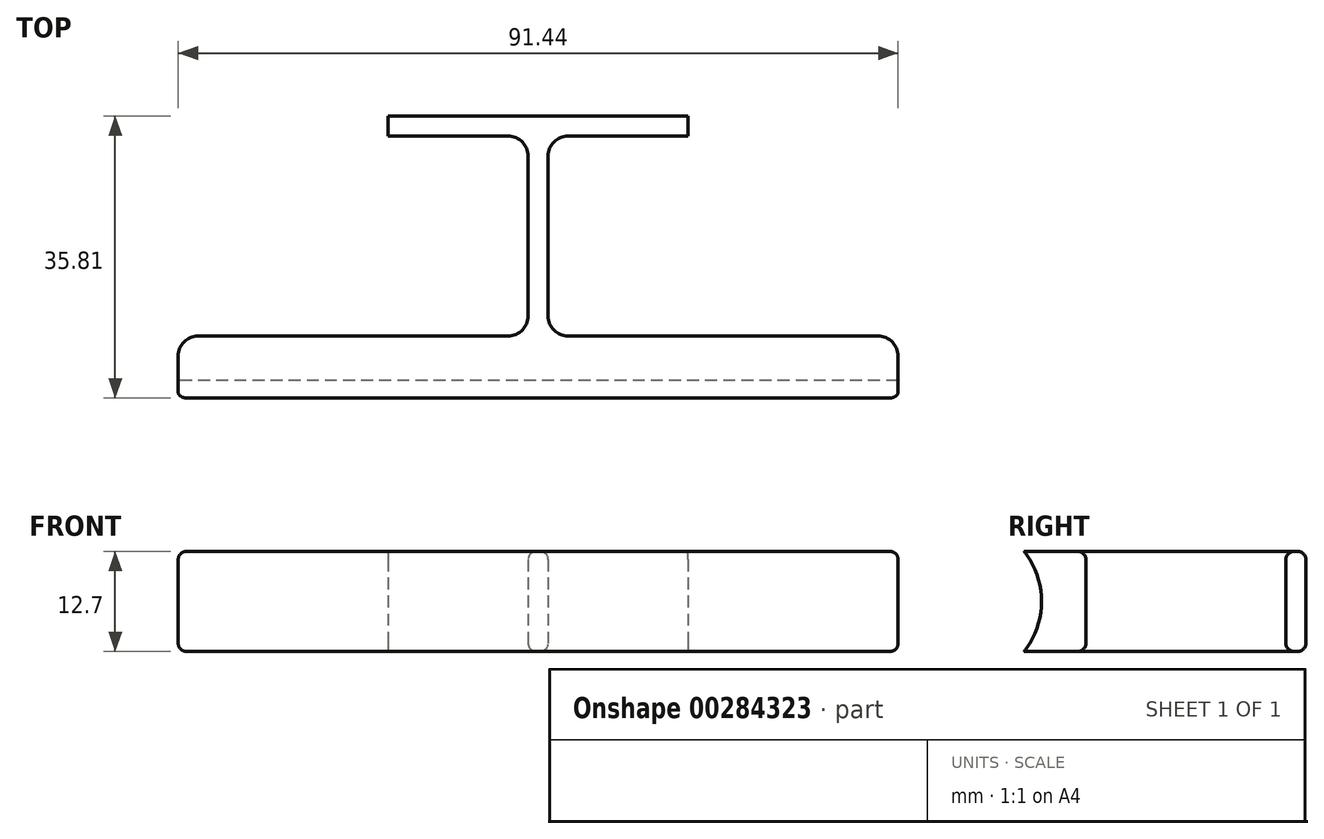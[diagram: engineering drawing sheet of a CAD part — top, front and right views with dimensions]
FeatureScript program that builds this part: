
annotation { "Feature Type Name" : "Feature", "Feature Type Description" : "" }
export const myFeature = defineFeature(function(context is Context, id is Id, definition is map)
    precondition{}
    {
        {
            var Q0;
            Q0=qCreatedBy(makeId("Top.planeOp"),FACE);
            var sketch = newSketch(context, id + "F0", { "sketchPlane" : qUnion([Q0])});
            skLineSegment(sketch, "E0", {"start": v(0, 0) * mm, "end": v(-19.05, 0) * mm});
            skLineSegment(sketch, "E1", {"start": v(0, 0) * mm, "end": v(19.05, 0) * mm});
            skLineSegment(sketch, "E2", {"start": v(-45.72, -27.94) * mm, "end": v(-45.72, -30.48) * mm});
            skLineSegment(sketch, "E3", {"start": v(-45.72, -30.48) * mm, "end": v(45.72, -30.48) * mm});
            skLineSegment(sketch, "E4", {"start": v(45.72, -30.48) * mm, "end": v(45.72, -27.94) * mm});
            skLineSegment(sketch, "E5", {"start": v(0, -30.48) * mm, "end": v(0, 0) * mm, "construction": true});
            skLineSegment(sketch, "E6.bottom", {"start": v(-19.05, -2.54) * mm, "end": v(-1.27, -2.54) * mm});
            skLineSegment(sketch, "E6.top", {"start": v(-45.72, -27.94) * mm, "end": v(-1.27, -27.94) * mm});
            skLineSegment(sketch, "E7", {"start": v(0, -2.54) * mm, "end": v(0, -27.94) * mm, "construction": true});
            skPoint(sketch, "E8", {"position": v(0, -15.24) * mm});
            skLineSegment(sketch, "E9.left", {"start": v(-1.27, -2.54) * mm, "end": v(-1.27, -27.94) * mm});
            skLineSegment(sketch, "E9.right", {"start": v(1.27, -2.54) * mm, "end": v(1.27, -27.94) * mm});
            skLineSegment(sketch, "E10", {"start": v(-1.27, -15.24) * mm, "end": v(1.27, -15.24) * mm, "construction": true});
            skLineSegment(sketch, "E11", {"start": v(-19.05, -2.54) * mm, "end": v(-19.05, 0) * mm});
            skLineSegment(sketch, "E12", {"start": v(19.05, 0) * mm, "end": v(19.05, -2.54) * mm});
            skLineSegment(sketch, "E13", {"start": v(-19.05, -1.27) * mm, "end": v(19.05, -1.27) * mm, "construction": true});
            skPoint(sketch, "E14", {"position": v(0, -1.27) * mm});
            skLineSegment(sketch, "E15.trimOffspring", {"start": v(1.27, -27.94) * mm, "end": v(45.72, -27.94) * mm});
            skLineSegment(sketch, "E16.trimOffspring", {"start": v(1.27, -2.54) * mm, "end": v(19.05, -2.54) * mm});
            skSolve(sketch);
        }
        {
            var Q0;
            Q0=makeQuery(id+"F0.imprint","IMPRINT",FACE,{"disambiguationData":[TD([[makeQuery(id+"F0.imprint","IMPRINT",EDGE,{"derivedFrom":sQuery(id+"F0.wireOp",EDGE,"E0")}),1.0]])]});
            extrude(context, id + "F1", {"entities" : qUnion([Q0]), "depth" : 12.7 * mm});
        }
        {
            var Q0;
            Q0=makeQuery(id+"F1.opExtrude","SWEPT_FACE",FACE,{"disambiguationData":[OSD([sQuery(id+"F0.wireOp",EDGE,"E4")])]});
            var sketch = newSketch(context, id + "F2", { "sketchPlane" : qUnion([Q0])});
            skLineSegment(sketch, "E17.0.0", {"start": v(-30.48, 0) * mm, "end": v(-27.94, 0) * mm});
            skLineSegment(sketch, "E17.0.2", {"start": v(-27.94, 12.7) * mm, "end": v(-30.48, 12.7) * mm});
            skLineSegment(sketch, "E17.0.3", {"start": v(-30.48, 12.7) * mm, "end": v(-30.48, 0) * mm});
            skLineSegment(sketch, "E18", {"start": v(-30.48, 0) * mm, "end": v(-35.8, 0) * mm});
            skLineSegment(sketch, "E19", {"start": v(-35.8, 0) * mm, "end": v(-30.48, 6.35) * mm});
            skLineSegment(sketch, "E20", {"start": v(-30.48, 6.35) * mm, "end": v(-35.8, 12.7) * mm});
            skLineSegment(sketch, "E21", {"start": v(-35.8, 12.7) * mm, "end": v(-30.48, 12.7) * mm});
            skSolve(sketch);
        }
        {
            var Q0;
            {var subQ2=sQuery(id+"F2.wireOp",EDGE,"E20");Q0=makeQuery(id+"F2.imprint","IMPRINT",FACE,{"disambiguationData":[TD([[makeQuery(id+"F2.imprint","IMPRINT",EDGE,{"derivedFrom":subQ2}),-1.0]])]});}
            var Q1;
            {var subQ0=sQuery(id+"F2.wireOp",EDGE,"E18");Q1=makeQuery(id+"F2.imprint","IMPRINT",FACE,{"disambiguationData":[TD([[makeQuery(id+"F2.imprint","IMPRINT",EDGE,{"derivedFrom":subQ0}),-1.0]])]});}
            var Q2;
            {var subQ0=sQuery(id+"F2.wireOp",EDGE,"DFXXT5Bl-ABkD-rZfx-TB3P-CU2xxBPRpCpw");var subQ1=sQuery(id+"F2.wireOp",EDGE,"E17.0.1");var subQ2=sQuery(id+"F2.wireOp",EDGE,"PkzQklKV-4UNx-XqyM-r72F-WXmGYkbQ70ns");var subQ3=sQuery(id+"F2.wireOp",EDGE,"ZFFAAHI1-nbwh-nJH1-ukWo-Dj7Sew2PWv25");Q2=makeQuery(id+"FTnoA9OfPemPWEm_1.1.Fb3Mo2sl9pyBsOD_1.boolean.opBoolean","MERGE",FACE,{"derivedFrom":[makeQuery(id+"F1.opExtrude","SWEPT_FACE",FACE,{"disambiguationData":[OSD([sQuery(id+"F0.wireOp",EDGE,"E2")])]}),makeQuery(id+"FTnoA9OfPemPWEm_1.1.Fb3Mo2sl9pyBsOD_1.opExtrude","CAP_FACE",FACE,{"disambiguationData":[OSD([subQ1,sQuery(id+"F2.wireOp",EDGE,"DQoqX5bU-sU3v-EXNl-5AFO-wBolTAnTBgKw"),subQ3])],"isStart":true}),makeQuery(id+"FTnoA9OfPemPWEm_1.1.Fb3Mo2sl9pyBsOD_1.opExtrude","CAP_FACE",FACE,{"disambiguationData":[OSD([subQ1,subQ3,subQ2])],"isStart":true}),makeQuery(id+"FTnoA9OfPemPWEm_1.1.Fb3Mo2sl9pyBsOD_1.opExtrude","CAP_FACE",FACE,{"disambiguationData":[OSD([subQ1,subQ2,subQ0])],"isStart":true}),makeQuery(id+"FTnoA9OfPemPWEm_1.1.Fb3Mo2sl9pyBsOD_1.opExtrude","CAP_FACE",FACE,{"disambiguationData":[OSD([subQ1,subQ0,sQuery(id+"F2.wireOp",EDGE,"Y51H4d37-WT34-3JM8-DEph-uDnF3JEXPVEw")])],"isStart":true})]});}
            extrude(context, id + "F3", {"entities" : qUnion([Q0, Q1]), "operationType" : NewBodyOperationType.ADD, "endBound" : BoundingType.UP_TO_SURFACE, "oppositeDirection" : true, "endBoundEntityFace" : qUnion([Q2]), "depth" : 101.6 * mm});
        }
        {
            var Q0;
            {var subQ0=sQuery(id+"F2.wireOp",EDGE,"E19");var subQ1=sQuery(id+"F2.wireOp",EDGE,"E17.0.3");var subQ2=sQuery(id+"F2.wireOp",EDGE,"E20");Q0=makeQuery(id+"F3.boolean.opBoolean","MERGE",EDGE,{"derivedFrom":[makeQuery(id+"F3.opExtrude","SWEPT_EDGE",EDGE,{"disambiguationData":[OSD([subQ1,subQ0,subQ2]),ownerDisambiguation([makeQuery(id+"F3.opExtrude","SWEPT_BODY",BODY,{"disambiguationData":[OSD([subQ1,subQ2,sQuery(id+"F2.wireOp",EDGE,"E21")])]})])]}),makeQuery(id+"F3.opExtrude","SWEPT_EDGE",EDGE,{"disambiguationData":[OSD([subQ1,subQ0,subQ2]),ownerDisambiguation([makeQuery(id+"F3.opExtrude","SWEPT_BODY",BODY,{"disambiguationData":[OSD([subQ1,sQuery(id+"F2.wireOp",EDGE,"E18"),subQ0])]})])]})]});}
            fillet(context, id + "F4", {"entities" : qUnion([Q0]), "radius" : 10.16 * mm, "tangentPropagation" : true, "allowEdgeOverflow" : false});
        }
        {
            var Q0;
            Q0=makeQuery(id+"F1.opExtrude","SWEPT_EDGE",EDGE,{"disambiguationData":[OSD([sQuery(id+"F0.wireOp",EDGE,"E6.bottom"),sQuery(id+"F0.wireOp",EDGE,"E9.left")])]});
            var Q1;
            Q1=makeQuery(id+"F1.opExtrude","SWEPT_EDGE",EDGE,{"disambiguationData":[OSD([sQuery(id+"F0.wireOp",EDGE,"E9.right"),sQuery(id+"F0.wireOp",EDGE,"E16.trimOffspring")])]});
            var Q2;
            Q2=makeQuery(id+"F1.opExtrude","SWEPT_EDGE",EDGE,{"disambiguationData":[OSD([sQuery(id+"F0.wireOp",EDGE,"E9.right"),sQuery(id+"F0.wireOp",EDGE,"E15.trimOffspring")])]});
            var Q3;
            Q3=makeQuery(id+"F1.opExtrude","SWEPT_EDGE",EDGE,{"disambiguationData":[OSD([sQuery(id+"F0.wireOp",EDGE,"E6.top"),sQuery(id+"F0.wireOp",EDGE,"E9.left")])]});
            var Q4;
            Q4=makeQuery(id+"F1.opExtrude","SWEPT_EDGE",EDGE,{"disambiguationData":[OSD([sQuery(id+"F0.wireOp",EDGE,"E2"),sQuery(id+"F0.wireOp",EDGE,"E6.top")])]});
            var Q5;
            Q5=makeQuery(id+"F1.opExtrude","SWEPT_EDGE",EDGE,{"disambiguationData":[OSD([sQuery(id+"F0.wireOp",EDGE,"E4"),sQuery(id+"F0.wireOp",EDGE,"E15.trimOffspring")])]});
            fillet(context, id + "F5", {"entities" : qUnion([Q0, Q1, Q2, Q3, Q4, Q5]), "radius" : 2.54 * mm, "tangentPropagation" : true, "allowEdgeOverflow" : false});
        }
        {
            var Q0;
            Q0=makeQuery(id+"F1.opExtrude","CAP_EDGE",EDGE,{"disambiguationData":[OSD([sQuery(id+"F0.wireOp",EDGE,"E9.left")])],"isStart":false});
            var Q1;
            Q1=makeQuery(id+"F1.opExtrude","CAP_EDGE",EDGE,{"disambiguationData":[OSD([sQuery(id+"F0.wireOp",EDGE,"E9.left")])],"isStart":true});
            var Q2;
            Q2=makeQuery(id+"F1.opExtrude","CAP_EDGE",EDGE,{"disambiguationData":[OSD([sQuery(id+"F0.wireOp",EDGE,"E9.right")])],"isStart":true});
            var Q3;
            Q3=makeQuery(id+"F1.opExtrude","CAP_EDGE",EDGE,{"disambiguationData":[OSD([sQuery(id+"F0.wireOp",EDGE,"E9.right")])],"isStart":false});
            var Q4;
            Q4=makeQuery(id+"F1.opExtrude","CAP_EDGE",EDGE,{"disambiguationData":[OSD([sQuery(id+"F0.wireOp",EDGE,"E0"),sQuery(id+"F0.wireOp",EDGE,"E1")])],"isStart":true});
            var Q5;
            Q5=makeQuery(id+"F1.opExtrude","CAP_EDGE",EDGE,{"disambiguationData":[OSD([sQuery(id+"F0.wireOp",EDGE,"E0"),sQuery(id+"F0.wireOp",EDGE,"E1")])],"isStart":false});
            fillet(context, id + "F6", {"entities" : qUnion([Q0, Q1, Q2, Q3, Q4, Q5]), "radius" : 1.02 * mm, "tangentPropagation" : true, "allowEdgeOverflow" : false});
        }
    });
